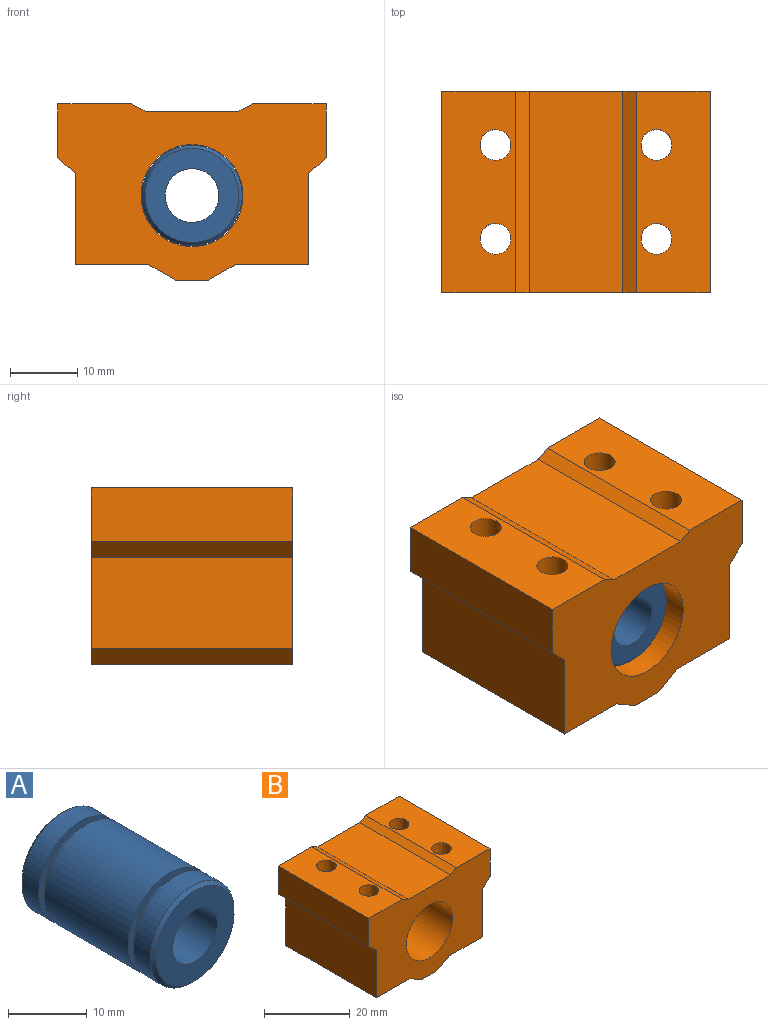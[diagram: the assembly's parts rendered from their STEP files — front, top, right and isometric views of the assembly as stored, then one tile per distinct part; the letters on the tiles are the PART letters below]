
ASSEMBLY  parts=2 mates=1
PART A: 14 faces, bbox 15x24x15 mm
  f0: plane 14x14mm, normal (0,-1,0), area 103.7mm2, adj f1,f13
  f1: cylinder r=4mm len=24mm, axis (0,1,0), area 603.2mm2, adj f0,f2
  f2: plane 14x14mm, normal (0,1,0), area 103.7mm2, adj f1,f3
  f3: cone r=7.5mm half-angle=45deg, axis (0,-1,0), area 32.2mm2, adj f2,f4
  f4: cylinder r=7.5mm len=15mm, axis (0,1,0), area 141.4mm2, adj f3,f5
  f5: plane 15x15mm, normal (0,-1,0), area 44mm2, adj f4,f6
  f6: cylinder r=6.5mm len=13mm, axis (0,1,0), area 40.8mm2, adj f5,f7
  f7: plane 15x15mm, normal (0,1,0), area 44mm2, adj f6,f8
  f8: cylinder r=7.5mm len=15mm, axis (0,1,0), area 706.9mm2, adj f7,f9
  f9: plane 15x15mm, normal (0,-1,0), area 44mm2, adj f8,f10
  f10: cylinder r=6.5mm len=13mm, axis (0,1,0), area 40.8mm2, adj f9,f11
  f11: plane 15x15mm, normal (0,1,0), area 44mm2, adj f10,f12
  f12: cylinder r=7.5mm len=15mm, axis (0,1,0), area 141.4mm2, adj f11,f13
  f13: cone r=7mm half-angle=45deg, axis (0,1,0), area 32.2mm2, adj f0,f12
PART B: 51 faces, bbox 40x30x26.3 mm
  f0: plane 30x11mm, normal (0,0,-1), area 210.7mm2, adj f10,f11,f21,f22,f23,f24,f25,f26
  f1: plane 30x11mm, normal (0,0,-1), area 210.7mm2, adj f13,f14,f21,f22,f37,f38,f39,f40
  f2: cylinder r=2.3mm len=21mm, axis (0,0,-1), area 303.5mm2, adj f17,f50
  f3: cylinder r=2.3mm len=21mm, axis (0,0,-1), area 303.5mm2, adj f17,f43
  f4: cylinder r=2.3mm len=21mm, axis (0,0,-1), area 303.5mm2, adj f7,f36
  f5: cylinder r=2.3mm len=21mm, axis (0,0,-1), area 303.5mm2, adj f7,f29
  f6: plane 30x2mm, normal (0.47,0,0.88), area 67.9mm2, adj f7,f20,f21,f22
  f7: plane 30x11mm, normal (0,0,1), area 296.8mm2, adj f4,f5,f6,f8,f21,f22
  f8: plane 30x8mm, normal (-1,0,0), area 240mm2, adj f7,f9,f21,f22
  f9: plane 30x2.58mm, normal (-0.68,0,-0.73), area 105.7mm2, adj f8,f10,f21,f22
  f10: plane 30x13.6mm, normal (-1,0,0), area 408mm2, adj f0,f9,f21,f22
  f11: plane 30x3.92mm, normal (-0.5,0,-0.87), area 135.8mm2, adj f0,f12,f21,f22
  f12: plane 30x5mm, normal (0,0,-1), area 150mm2, adj f11,f13,f21,f22
  f13: plane 30x3.92mm, normal (0.5,0,-0.87), area 135.8mm2, adj f1,f12,f21,f22
  f14: plane 30x13.6mm, normal (1,0,0), area 408mm2, adj f1,f15,f21,f22
  f15: plane 30x2.58mm, normal (0.68,0,-0.73), area 105.7mm2, adj f14,f16,f21,f22
  f16: plane 30x8mm, normal (1,0,0), area 240mm2, adj f15,f17,f21,f22
  f17: plane 30x11mm, normal (0,0,1), area 296.8mm2, adj f2,f3,f16,f18,f21,f22
  f18: plane 30x2mm, normal (-0.47,0,0.88), area 67.9mm2, adj f17,f20,f21,f22
  f19: cylinder r=7.6mm len=30mm, axis (0,1,0), area 1432.6mm2, adj f21,f22
  f20: plane 30x14mm, normal (0,0,1), area 420mm2, adj f6,f18,f21,f22
  f21: plane 40x26.26mm, normal (0,-1,0), area 705.3mm2, adj f0,f1,f6,f7,f8,f9,f10,f11
  f22: plane 40x26.26mm, normal (0,1,0), area 705.3mm2, adj f0,f1,f6,f7,f8,f9,f10,f11
  f23: plane 4.79x3mm, normal (-1,0,0), area 14.4mm2, adj f0,f24,f28,f29
  f24: plane 4.15x3mm, normal (-0.5,0.87,0), area 14.4mm2, adj f0,f23,f25,f29
  f25: plane 4.15x3mm, normal (0.5,0.87,0), area 14.4mm2, adj f0,f24,f26,f29
  f26: plane 4.79x3mm, normal (1,0,0), area 14.4mm2, adj f0,f25,f27,f29
  f27: plane 4.15x3mm, normal (0.5,-0.87,0), area 14.4mm2, adj f0,f26,f28,f29
  f28: plane 4.15x3mm, normal (-0.5,-0.87,0), area 14.4mm2, adj f0,f23,f27,f29
  f29: plane 9.58x8.3mm, normal (0,0,-1), area 43mm2, adj f5,f23,f24,f25,f26,f27,f28
  f30: plane 4.15x3mm, normal (-0.5,-0.87,0), area 14.4mm2, adj f0,f31,f35,f36
  f31: plane 4.79x3mm, normal (-1,0,0), area 14.4mm2, adj f0,f30,f32,f36
  f32: plane 4.15x3mm, normal (-0.5,0.87,0), area 14.4mm2, adj f0,f31,f33,f36
  f33: plane 4.15x3mm, normal (0.5,0.87,0), area 14.4mm2, adj f0,f32,f34,f36
  f34: plane 4.79x3mm, normal (1,0,0), area 14.4mm2, adj f0,f33,f35,f36
  f35: plane 4.15x3mm, normal (0.5,-0.87,0), area 14.4mm2, adj f0,f30,f34,f36
  f36: plane 9.58x8.3mm, normal (0,0,-1), area 43mm2, adj f4,f30,f31,f32,f33,f34,f35
  f37: plane 4.15x3mm, normal (-0.5,0.87,0), area 14.4mm2, adj f1,f38,f42,f43
  f38: plane 4.15x3mm, normal (0.5,0.87,0), area 14.4mm2, adj f1,f37,f39,f43
  f39: plane 4.79x3mm, normal (1,0,0), area 14.4mm2, adj f1,f38,f40,f43
  f40: plane 4.15x3mm, normal (0.5,-0.87,0), area 14.4mm2, adj f1,f39,f41,f43
  f41: plane 4.15x3mm, normal (-0.5,-0.87,0), area 14.4mm2, adj f1,f40,f42,f43
  f42: plane 4.79x3mm, normal (-1,0,0), area 14.4mm2, adj f1,f37,f41,f43
  f43: plane 9.58x8.3mm, normal (0,0,-1), area 43mm2, adj f3,f37,f38,f39,f40,f41,f42
  f44: plane 4.15x3mm, normal (-0.5,0.87,0), area 14.4mm2, adj f1,f45,f49,f50
  f45: plane 4.15x3mm, normal (0.5,0.87,0), area 14.4mm2, adj f1,f44,f46,f50
  f46: plane 4.79x3mm, normal (1,0,0), area 14.4mm2, adj f1,f45,f47,f50
  f47: plane 4.15x3mm, normal (0.5,-0.87,0), area 14.4mm2, adj f1,f46,f48,f50
  f48: plane 4.15x3mm, normal (-0.5,-0.87,0), area 14.4mm2, adj f1,f47,f49,f50
  f49: plane 4.79x3mm, normal (-1,0,0), area 14.4mm2, adj f1,f44,f48,f50
  f50: plane 9.58x8.3mm, normal (0,0,-1), area 43mm2, adj f2,f44,f45,f46,f47,f48,f49
PLACE A rot(axis=(0,-1,0),77.3deg) t=(-11.53,-20.75,-2.33)mm
PLACE B t=(-11.53,-5.75,-2.33)mm fixed
MATE revolute A.f1 <-> B.f19  axis (0,1,0) through (-11.53,-20.75,-2.33)mm
